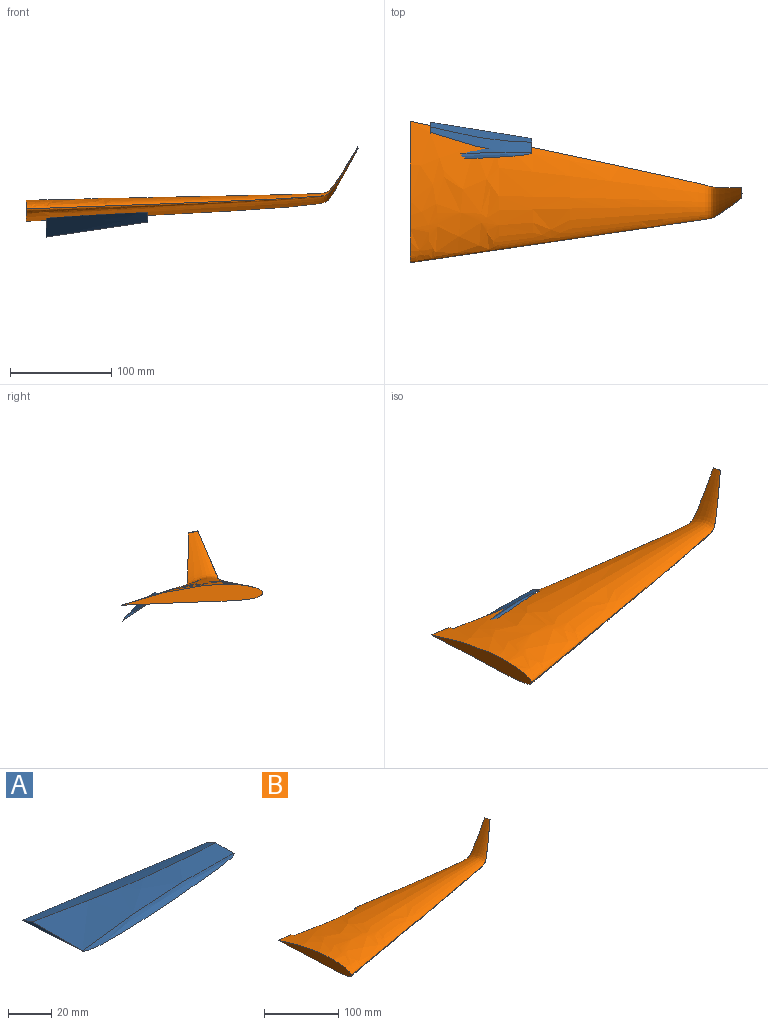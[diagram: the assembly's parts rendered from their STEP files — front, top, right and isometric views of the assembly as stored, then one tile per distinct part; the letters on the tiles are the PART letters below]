
ASSEMBLY  parts=2 mates=1
PART A: 6 faces, bbox 127.1x74.7x15.7 mm
  f0: plane 39.75x2.55mm, normal (-1,0,0), area 35.6mm2, adj f3,f4,f5
  f1: plane 17.78x3.08mm, normal (1,0,0), area 15.6mm2, adj f3,f4,f5
  f2: bspline ~100x11.84mm, area 434.4mm2, adj f3,f5
  f3: bspline ~100x50.7mm, area 1951.6mm2, adj f0,f1,f2,f4
  f4: bspline ~126.79x42.54mm, area 1000.1mm2, adj f0,f1,f3,f5
  f5: bspline ~126.97x67.79mm, area 3290.4mm2, adj f0,f1,f2,f4
PART B: 8 faces, bbox 328.7x147.6x74.5 mm
  f0: bspline ~327.1x139.47mm, area 26968.9mm2, adj f1,f2,f3,f4,f6,f7
  f1: plane 17.78x3.08mm, normal (-1,0,0), area 15.6mm2, adj f0,f4,f7
  f2: plane 10.04x2.14mm, normal (0.34,0.18,0.92), area 4.1mm2, adj f0,f4
  f3: plane 140.77x22.01mm, normal (-1,0,0), area 1600.7mm2, adj f0,f4
  f4: bspline ~327.38x139.47mm, area 24021.1mm2, adj f0,f1,f2,f3,f5,f6
  f5: bspline ~100x5.83mm, area 0mm2, adj f4,f7
  f6: plane 39.75x2.55mm, normal (1,0,0), area 35.6mm2, adj f0,f4,f7
  f7: bspline ~100x50.7mm, area 2240.8mm2, adj f0,f1,f5,f6
PLACE A rot(axis=(-1,0,0),30deg) t=(0,10.68,0.56)mm
PLACE B at identity fixed
MATE fastened B.f6 <-> A.f0  axis (1,0,0) through (20,20.72,-3.49)mm
